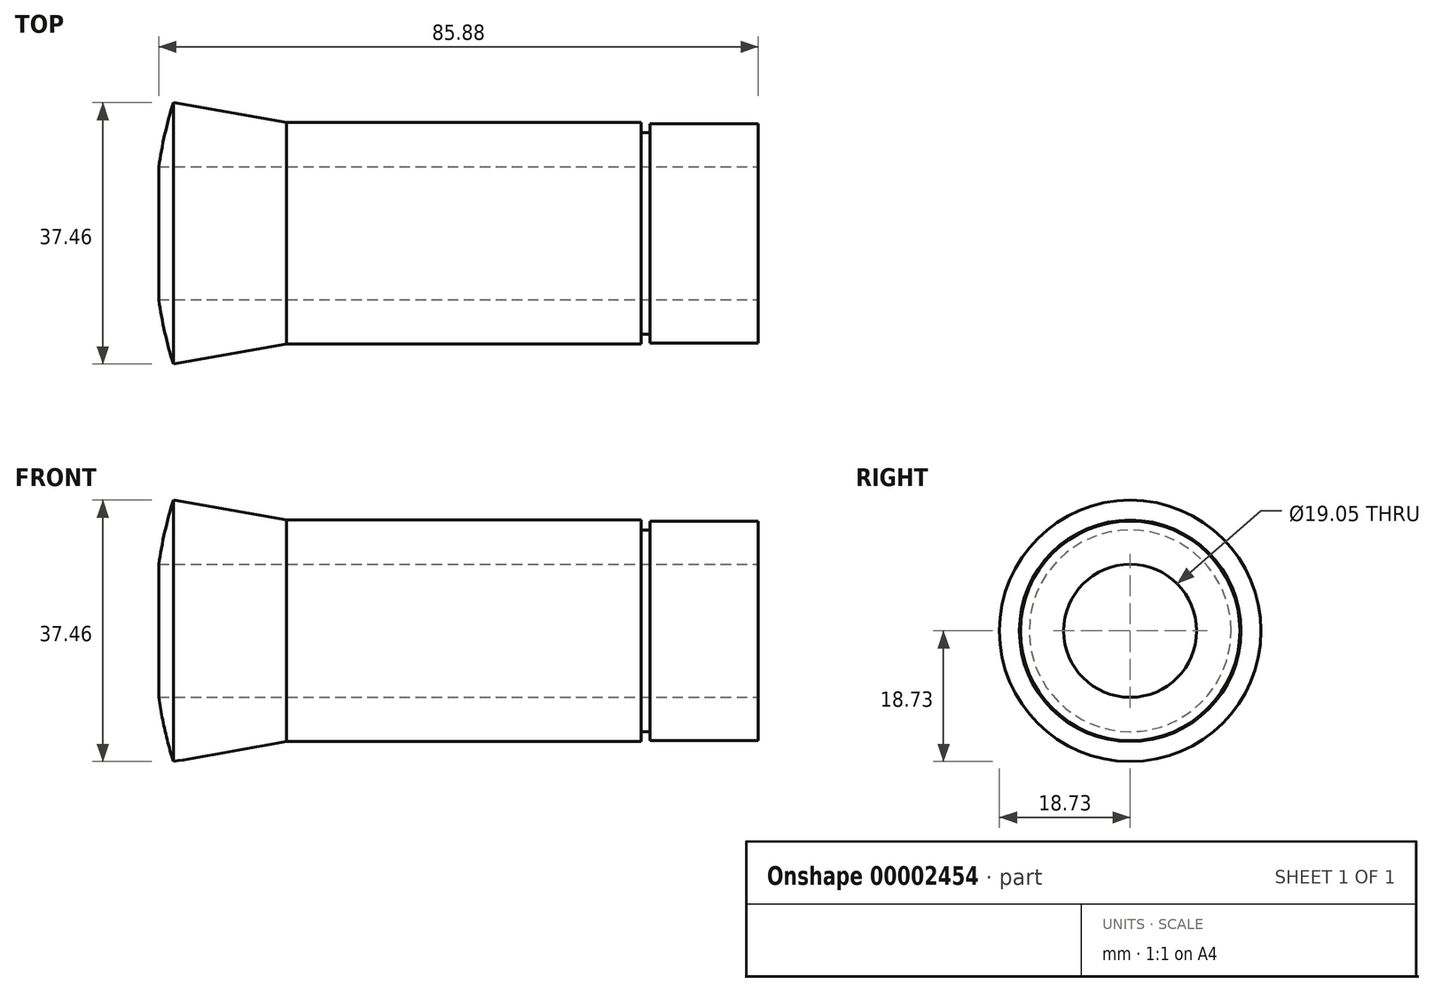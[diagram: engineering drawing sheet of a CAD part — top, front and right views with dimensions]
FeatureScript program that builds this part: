
annotation { "Feature Type Name" : "Feature", "Feature Type Description" : "" }
export const myFeature = defineFeature(function(context is Context, id is Id, definition is map)
    precondition{}
    {
        {
            var Q0;
            Q0=qCreatedBy(makeId("Front.planeOp"),FACE);
            var sketch = newSketch(context, id + "F0", { "sketchPlane" : qUnion([Q0])});
            skPoint(sketch, "E0.rect.middle", {"position": v(0, 0) * mm});
            skLineSegment(sketch, "E1", {"start": v(-36.2, 18.73) * mm, "end": v(-19.98, 15.87) * mm});
            skLineSegment(sketch, "E2", {"start": v(0, 0) * mm, "end": v(-50.87, 0) * mm, "construction": true});
            skLineSegment(sketch, "E3.trimOffspring", {"start": v(-19.98, 15.87) * mm, "end": v(30.82, 15.88) * mm});
            skPoint(sketch, "E0.rect.top.end.orphan", {"position": v(36.2, -18.73) * mm});
            skLineSegment(sketch, "E4", {"start": v(47.58, 15.72) * mm, "end": v(47.58, 0) * mm});
            skLineSegment(sketch, "E5", {"start": v(47.58, 15.72) * mm, "end": v(32.09, 15.72) * mm});
            skLineSegment(sketch, "E6", {"start": v(30.82, 15.72) * mm, "end": v(30.82, 15.88) * mm});
            skLineSegment(sketch, "E7", {"start": v(30.82, 15.72) * mm, "end": v(30.82, 14.45) * mm});
            skLineSegment(sketch, "E8", {"start": v(30.82, 14.45) * mm, "end": v(32.09, 14.45) * mm});
            skLineSegment(sketch, "E9", {"start": v(32.09, 14.45) * mm, "end": v(32.09, 15.72) * mm});
            skLineSegment(sketch, "E10", {"start": v(-36.2, 0) * mm, "end": v(47.58, 0) * mm});
            skArc(sketch, "E11", {"start": v(-36.2, 18.73) * mm, "mid": v(-38.3, 9.47) * mm, "end": v(-39.02, 0) * mm});
            skLineSegment(sketch, "E12", {"start": v(-36.2, 0) * mm, "end": v(-39.02, 0) * mm});
            skSolve(sketch);
        }
        {
            var Q0;
            Q0=makeQuery(id+"F0.imprint","IMPRINT",FACE,{"disambiguationData":[TD([[makeQuery(id+"F0.imprint","IMPRINT",EDGE,{"derivedFrom":sQuery(id+"F0.wireOp",EDGE,"E1")}),-1.0]])]});
            var Q1;
            Q1=sQuery(id+"F0.wireOp",EDGE,"E2");
            revolve(context, id + "F1", {"entities" : qUnion([Q0]), "axis" : qUnion([Q1]), "revolveType" : RevolveType.FULL});
        }
        {
            var Q0;
            Q0=makeQuery(id+"F1.opRevolve","SWEPT_FACE",FACE,{"disambiguationData":[OSD([sQuery(id+"F0.wireOp",EDGE,"E4")])]});
            var sketch = newSketch(context, id + "F2", { "sketchPlane" : qUnion([Q0])});
            skCircle(sketch, "E13", {"center": v(0, 0) * mm, "radius": 9.53 * mm});
            skSolve(sketch);
        }
        {
            var Q0;
            Q0=makeQuery(id+"F2.imprint","IMPRINT",FACE,{"disambiguationData":[TD([[makeQuery(id+"F2.imprint","IMPRINT",EDGE,{"derivedFrom":sQuery(id+"F2.wireOp",EDGE,"E13")}),1.0]])]});
            extrude(context, id + "F3", {"entities" : qUnion([Q0]), "operationType" : NewBodyOperationType.REMOVE, "endBound" : BoundingType.THROUGH_ALL, "oppositeDirection" : true, "depth" : 25.4 * mm});
        }
    });
